# Revit family: Zahnplatte 2-Loch
name_source: partatom
category: HLS-Bauteile
revit_build: Autodesk Revit 2017 (Build: 20190507_1515(x64)
units: mm (PartAtom-declared; Revit-internal decimal feet)

## family parameters
Arbeitsebenenbasiert = Ja
Beim Laden mit Abzugskörper schneiden = Nein
Bemaßung runder Anschluss = Durchmesser verwenden
Gemeinsam genutzt = Ja
Immer vertikal = Nein
Raumberechnungspunkt = Nein
Teiletyp = Normal

## types (1)
- Zahnplatte 2-Loch
    Abmessung = 55 x 35 x 8 mm
    Anzugsmoment = 0.00 kN-m
    Artikelnummer = 0818110
    B = 35 mm  [stored 0.114829 ft]
    Breite = 35 mm  [stored 0.114829 ft]
    EAN = 4250928420619
    Fabrikat = MEFA
    Firma = MEFA Befestigungs- und Montagesysteme GmbH
    Form = vierkant
    Gewicht = 0.11 kg
    Gewicht pro Bauteil = 0.11 kg
    Gewinde = M12
    Kurztext1 = Zahnplatte 2-Loch
    Kurztext2 = M12 55 x 35 mm gvz
    L = 55 mm  [stored 0.180446 ft]
    Länge = 55 mm  [stored 0.180446 ft]
    Material = Stahl
    Mengeneinheit = St
    Oberflaeche = galvanisch verzinkt
    Profil = C-Profil
    Profiltyp = 45
    S = 8 mm  [stored 0.0262467 ft]
    Schienenbreite = 45 mm
    Stärke Material = 8 mm  [stored 0.0262467 ft]
    Vorgabe-Ansicht = 1219 mm
    vpe = 50 St

note: [stored X ft] marks values corroborated as IEEE doubles in the binary element streams (Revit-internal decimal feet)
